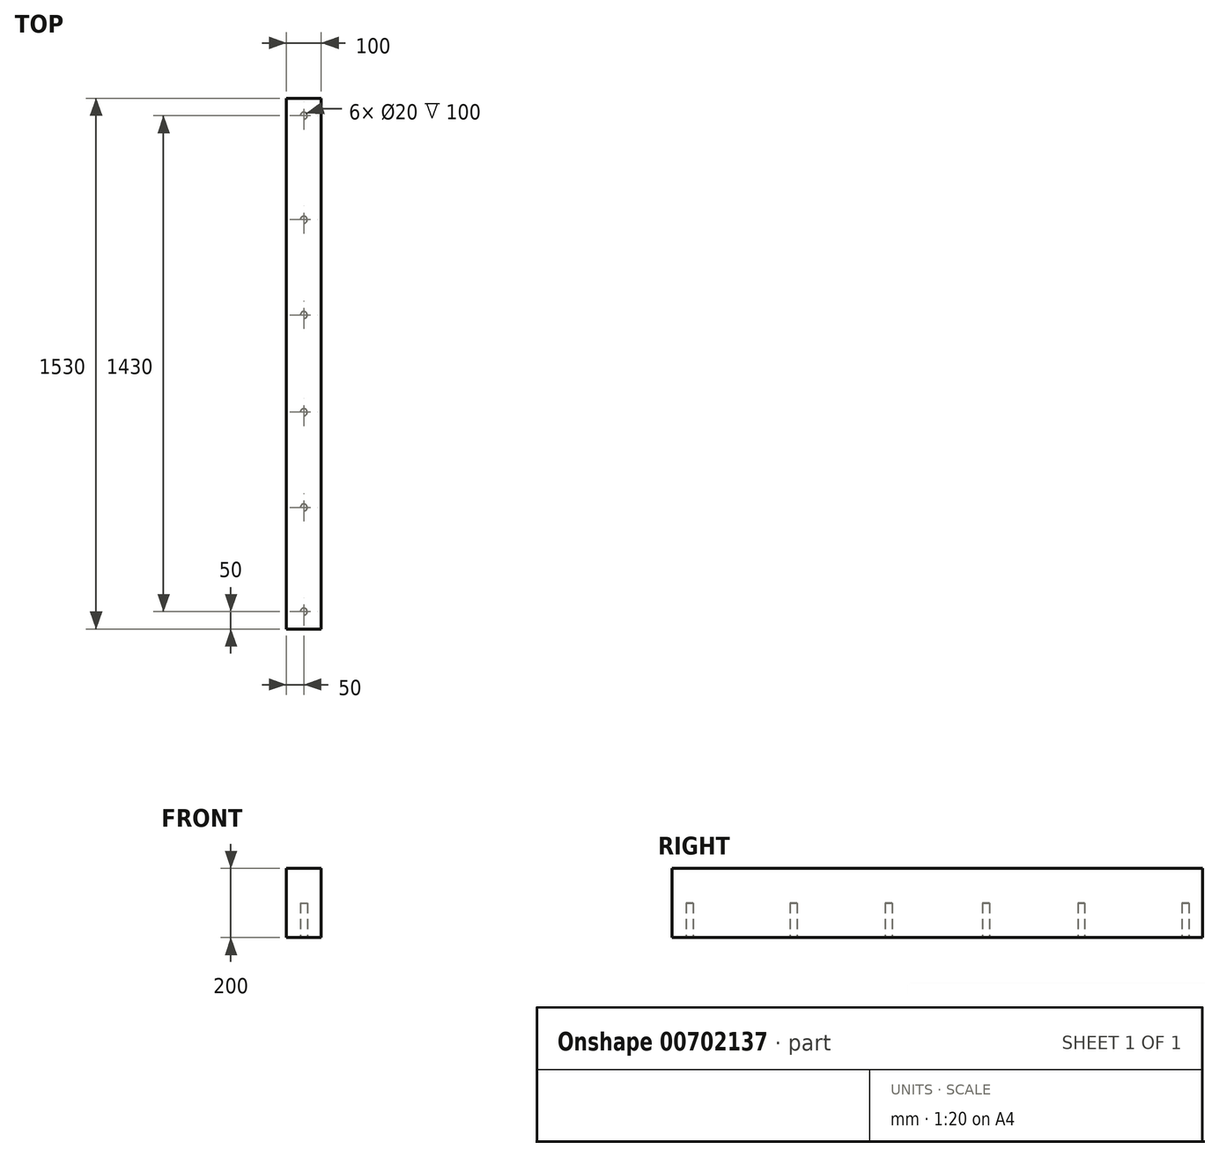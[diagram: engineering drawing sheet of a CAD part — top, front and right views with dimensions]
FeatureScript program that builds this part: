
annotation { "Feature Type Name" : "Feature", "Feature Type Description" : "" }
export const myFeature = defineFeature(function(context is Context, id is Id, definition is map)
    precondition{}
    {
        {
            var Q0;
            Q0=qCreatedBy(makeId("Front.planeOp"),FACE);
            var sketch = newSketch(context, id + "F0", { "sketchPlane" : qUnion([Q0])});
            skLineSegment(sketch, "E0.bottom", {"start": v(0, 0) * mm, "end": v(-100, 0) * mm});
            skLineSegment(sketch, "E0.top", {"start": v(0, 200) * mm, "end": v(-100, 200) * mm});
            skLineSegment(sketch, "E0.left", {"start": v(0, 0) * mm, "end": v(0, 200) * mm});
            skLineSegment(sketch, "E0.right", {"start": v(-100, 0) * mm, "end": v(-100, 200) * mm});
            skSolve(sketch);
        }
        {
            var Q0;
            Q0 = qSketchRegion(id + "F0", true);
            extrude(context, id + "F1", {"entities" : qUnion([Q0]), "depth" : 1530 * mm, "offsetDistance" : 25 * mm});
        }
        {
            var Q0;
            Q0=makeQuery(id+"F1.opExtrude","SWEPT_FACE",FACE,{"disambiguationData":[OSD([sQuery(id+"F0.wireOp",EDGE,"E0.bottom")])]});
            var sketch = newSketch(context, id + "F2", { "sketchPlane" : qUnion([Q0])});
            skCircle(sketch, "E1", {"center": v(-50, 1180) * mm, "radius": 10 * mm});
            skPoint(sketch, "E1.centerSnap0", {"position": v(-50, 1530) * mm});
            skCircle(sketch, "E2", {"center": v(-50, 905) * mm, "radius": 10 * mm});
            skCircle(sketch, "E3", {"center": v(-50, 625) * mm, "radius": 10 * mm});
            skCircle(sketch, "E4", {"center": v(-50, 350) * mm, "radius": 10 * mm});
            skCircle(sketch, "E5", {"center": v(-50, 1480) * mm, "radius": 10 * mm});
            skCircle(sketch, "E6", {"center": v(-50, 50) * mm, "radius": 10 * mm});
            skPoint(sketch, "E6.centerSnap0", {"position": v(-50, 0) * mm});
            skSolve(sketch);
        }
        {
            var Q0;
            Q0 = qSketchRegion(id + "F2", true);
            extrude(context, id + "F3", {"entities" : qUnion([Q0]), "operationType" : NewBodyOperationType.REMOVE, "oppositeDirection" : true, "depth" : 100 * mm, "offsetDistance" : 25 * mm});
        }
    });
